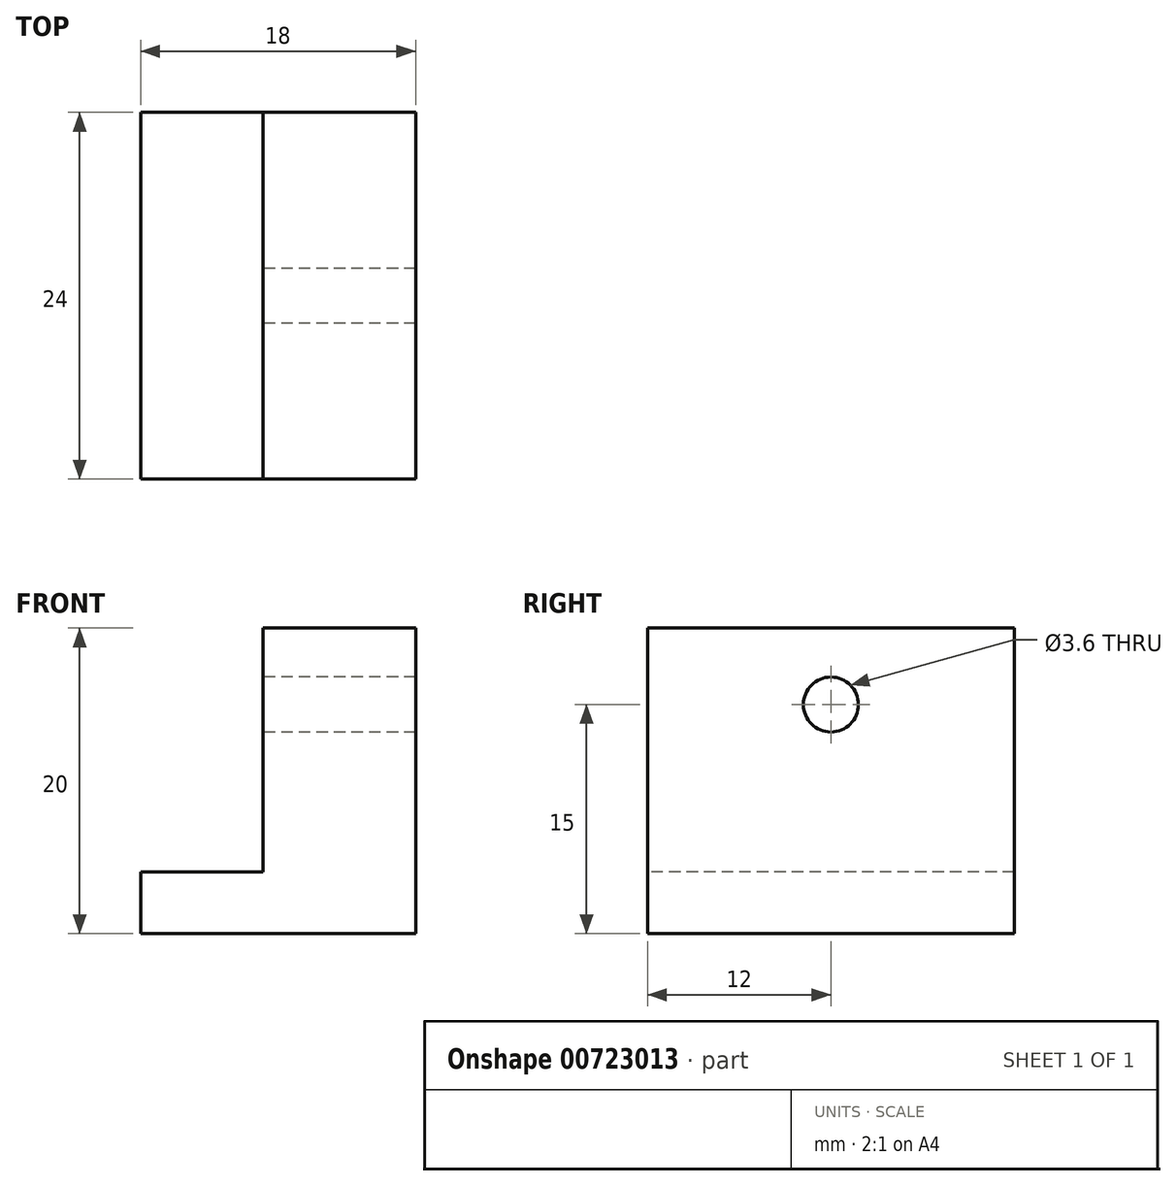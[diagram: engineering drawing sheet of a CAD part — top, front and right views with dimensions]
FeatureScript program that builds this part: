
annotation { "Feature Type Name" : "Feature", "Feature Type Description" : "" }
export const myFeature = defineFeature(function(context is Context, id is Id, definition is map)
    precondition{}
    {
        {
            var Q0;
            Q0=qCreatedBy(makeId("Front.planeOp"),FACE);
            var sketch = newSketch(context, id + "F0", { "sketchPlane" : qUnion([Q0])});
            skLineSegment(sketch, "E0.bottom", {"start": v(5, 5) * mm, "end": v(-5, 5) * mm});
            skLineSegment(sketch, "E0.top", {"start": v(5, -5) * mm, "end": v(-5, -5) * mm});
            skLineSegment(sketch, "E0.left", {"start": v(5, 5) * mm, "end": v(5, -5) * mm});
            skLineSegment(sketch, "E0.right", {"start": v(-5, 5) * mm, "end": v(-5, -5) * mm});
            skPoint(sketch, "E0.middle", {"position": v(0, 0) * mm});
            skSolve(sketch);
        }
        {
            var Q0;
            Q0 = qSketchRegion(id + "F0", true);
            extrude(context, id + "F1", {"entities" : qUnion([Q0]), "depth" : 24 * mm, "offsetDistance" : 25 * mm});
        }
        {
            var Q0;
            Q0=makeQuery(id+"F1.opExtrude","SWEPT_FACE",FACE,{"disambiguationData":[OSD([sQuery(id+"F0.wireOp",EDGE,"E0.right")])]});
            var sketch = newSketch(context, id + "F2", { "sketchPlane" : qUnion([Q0])});
            skLineSegment(sketch, "E1", {"start": v(0, 0) * mm, "end": v(24, 0) * mm});
            skLineSegment(sketch, "E2", {"start": v(24, 0) * mm, "end": v(12, -5) * mm});
            skLineSegment(sketch, "E3", {"start": v(12, -5) * mm, "end": v(12, 0) * mm});
            skSolve(sketch);
        }
        {
            var Q0;
            Q0=sQuery(id+"F2.wireOp",VERTEX,"E3.end");
            var Q1;
            Q1=makeQuery(id+"F1.opExtrude","SWEPT_BODY",BODY,{"disambiguationData":[OSD([sQuery(id+"F0.wireOp",EDGE,"E0.bottom"),sQuery(id+"F0.wireOp",EDGE,"E0.top"),sQuery(id+"F0.wireOp",EDGE,"E0.left"),sQuery(id+"F0.wireOp",EDGE,"E0.right")])]});
            hole(context, id + "F3", {"style" : HoleStyle.SIMPLE, "endStyle" : HoleEndStyle.THROUGH, "holeDiameter" : 3.6 * mm, "majorDiameter" : 5 * mm, "isTappedThrough" : true, "tappedDepth" : 12 * mm, "tapClearance" : 3, "locations" : qUnion([Q0]), "scope" : qUnion([Q1])});
        }
        {
            var Q0;
            Q0=makeQuery(id+"F1.opExtrude","SWEPT_FACE",FACE,{"disambiguationData":[OSD([sQuery(id+"F0.wireOp",EDGE,"E0.top")])]});
            extrude(context, id + "F4", {"entities" : qUnion([Q0]), "operationType" : NewBodyOperationType.ADD, "depth" : 10 * mm, "offsetDistance" : 25 * mm});
        }
        {
            var Q0;
            {var subQ0=sQuery(id+"F0.wireOp",EDGE,"E0.right");Q0=makeQuery(id+"F4.boolean.opBoolean","MERGE",FACE,{"derivedFrom":[makeQuery(id+"F1.opExtrude","SWEPT_FACE",FACE,{"disambiguationData":[OSD([subQ0])]}),makeQuery(id+"F4.opExtrude","SWEPT_FACE",FACE,{"disambiguationData":[OSD([sQuery(id+"F0.wireOp",EDGE,"E0.top"),subQ0])]})]});}
            var sketch = newSketch(context, id + "F5", { "sketchPlane" : qUnion([Q0])});
            skLineSegment(sketch, "E4", {"start": v(0, -10.97) * mm, "end": v(24, -10.97) * mm});
            skSolve(sketch);
        }
        {
            var Q0;
            {var subQ0=sQuery(id+"F5.wireOp",EDGE,"E4");Q0=makeQuery(id+"F5.imprint","IMPRINT",FACE,{"disambiguationData":[TD([[makeQuery(id+"F5.imprint","IMPRINT",EDGE,{"derivedFrom":subQ0}),-1.0]])]});}
            extrude(context, id + "F6", {"entities" : qUnion([Q0]), "operationType" : NewBodyOperationType.ADD, "depth" : 6.5 * mm, "offsetDistance" : 25 * mm});
        }
        {
            var Q0;
            Q0=makeQuery(id+"F6.opExtrude","CAP_FACE",FACE,{"disambiguationData":[OSD([sQuery(id+"F0.wireOp",EDGE,"E0.top"),sQuery(id+"F0.wireOp",EDGE,"E0.right"),sQuery(id+"F5.wireOp",EDGE,"E4")])],"isStart":false});
            extrude(context, id + "F7", {"entities" : qUnion([Q0]), "operationType" : NewBodyOperationType.ADD, "depth" : 1.5 * mm, "offsetDistance" : 25 * mm});
        }
    });
